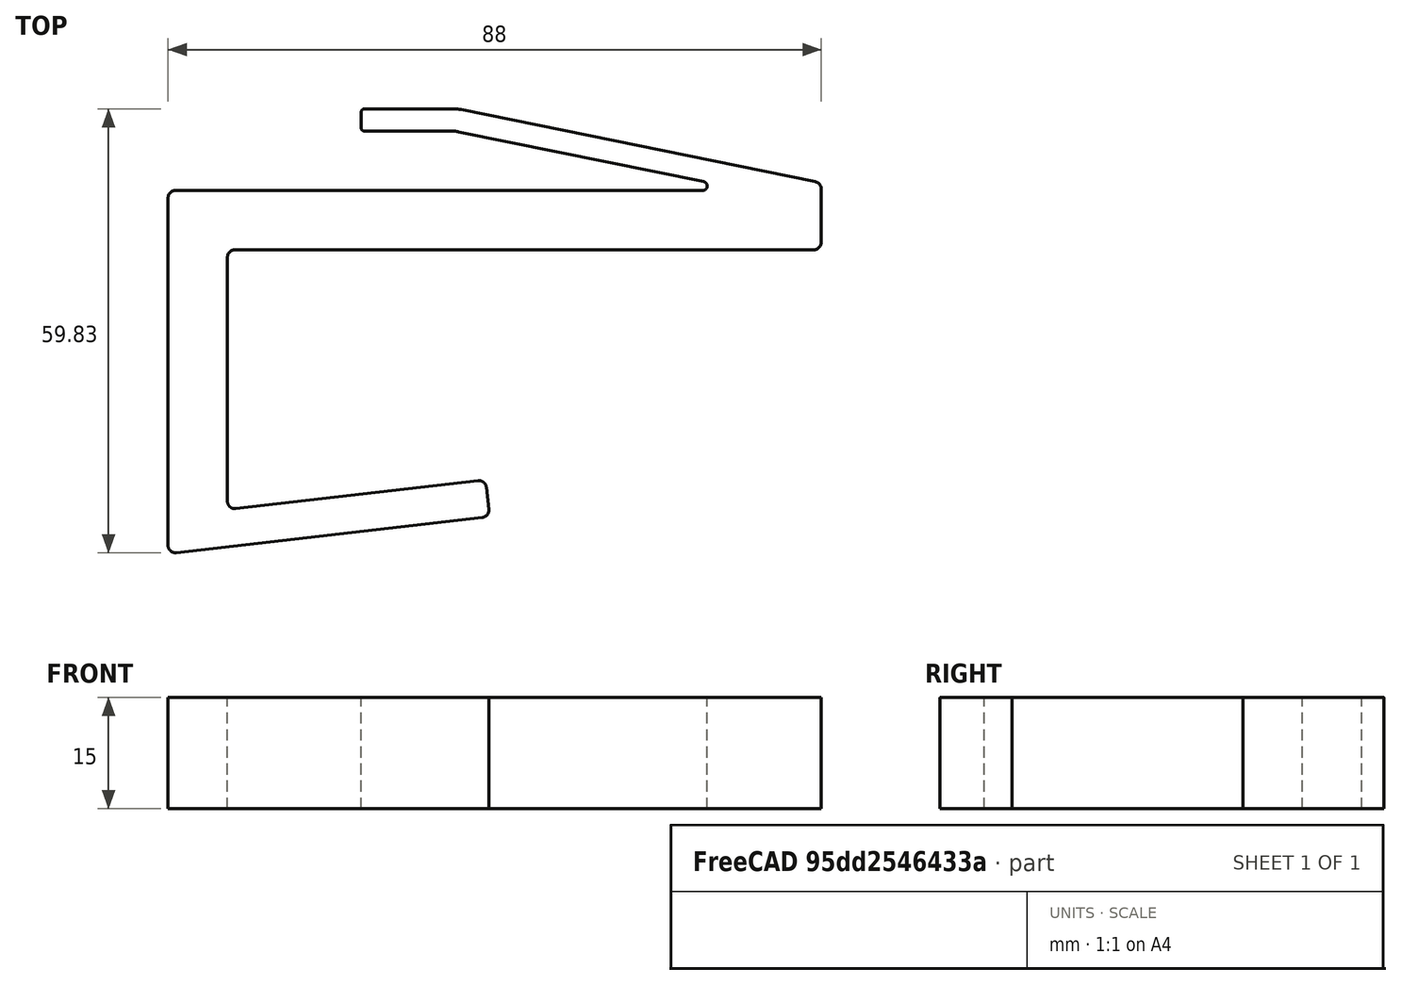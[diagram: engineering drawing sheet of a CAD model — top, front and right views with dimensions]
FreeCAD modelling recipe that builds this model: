
FCSTD DOCUMENT  (FreeCAD 0.16R)
Label: ClosetDoorLatch
License: All rights reserved
LicenseURL: http://en.wikipedia.org/wiki/All_rights_reserved
objects: PartDesign::Fillet×6, Sketcher::SketchObject×1, PartDesign::Pad×1, Mesh::Feature×1
note: 9 computed .brp shape members not serialized (recipe doc carries the construction recipe); baked Part::Feature solids carry a one-line shape summary decoded from their .brp

FEATURE [Sketcher::SketchObject] Sketch
  sketch-geometry (13):
    g0: LineSegment StartX=-8 StartY=8 StartZ=0 EndX=70 EndY=8 EndZ=0
    g1: LineSegment StartX=18 StartY=16 StartZ=0 EndX=18 EndY=19 EndZ=0
    g2: LineSegment StartX=18 StartY=19 StartZ=0 EndX=31 EndY=19 EndZ=0
    g3: LineSegment StartX=31 StartY=19 StartZ=0 EndX=80 EndY=9.02601 EndZ=0
    g4: LineSegment StartX=80 StartY=9.02601 StartZ=0 EndX=80 EndY=0 EndZ=0
    g5: LineSegment StartX=-8 StartY=-40.9533 StartZ=0 EndX=35.3421 EndY=-35.9672 EndZ=0
    g6: LineSegment StartX=35.3421 StartY=-35.9672 StartZ=0 EndX=34.7707 EndY=-31 EndZ=0
    g7: LineSegment StartX=34.7707 StartY=-31 StartZ=0 EndX=0 EndY=-35 EndZ=0
    g8: LineSegment StartX=0 StartY=-35 StartZ=0 EndX=0 EndY=0 EndZ=0
    g9: LineSegment StartX=0 StartY=0 StartZ=0 EndX=80 EndY=0 EndZ=0
    g10: LineSegment StartX=-8 StartY=8 StartZ=0 EndX=-8 EndY=-40.9533 EndZ=0
    g11: LineSegment StartX=18 StartY=16 StartZ=0 EndX=30.6978 EndY=16 EndZ=0
    g12: LineSegment StartX=30.6978 StartY=16 StartZ=0 EndX=70 EndY=8 EndZ=0
  constraints (39):
    c: PointOnObject(g4,g-1)
    c: Horizontal(g0)
    c: Coincident(g1,g2)
    c: Coincident(g2,g3)
    c: Distance(g1) = 3
    c: Vertical(g4)
    c: DistanceX(g4) = 80
    c: DistanceX(g1) = 18
    c: Vertical(g1)
    c: Distance(g2) = 13
    c: Coincident(g5,g6)
    c: Coincident(g6,g7)
    c: Coincident(g7,g8)
    c: Coincident(g8,g9)
    c: Coincident(g9,g4)
    c: Coincident(g10,g0)
    c: Coincident(g5,g10)
    c: Vertical(g10)
    c: Vertical(g8)
    c: Distance(g8,g10) = 8
    c: Distance(g8,g0) = 8
    c: PointOnObject(g8,g-1)
    c: Distance(g5,g7) = 5
    c: Distance(g6,g9) = 31
    c: Distance(g8) = 35
    c: Perpendicular(g6,g5)
    c: Distance(g7) = 35
    c: Coincident(g1,g11)
    c: Horizontal(g11)
    c: Coincident(g11,g12)
    c: Coincident(g12,g0)
    c: Distance(g1,g9) = 16
    c: Distance(g11,g2) = 3
    c: Parallel(g12,g3)
    c: Coincident(g4,g3)
    c: PointOnObject(g8,g-2)
    c: Distance(g0,g3) = 3
    c: Parallel(g5,g7)
    c: Distance(g0,g4) = 10
FEATURE [PartDesign::Pad] Pad
  Length = 15
  Length2 = 100
  Sketch = -> Sketch
  Type = 0
FEATURE [PartDesign::Fillet] Fillet
  Base = -> Pad [Edge2,Edge23,Edge20,Edge1,Edge32,Edge26,Edge29]
  Radius = 1
FEATURE [PartDesign::Fillet] Fillet001
  Base = -> Fillet [Edge45]
  Radius = 0.6
FEATURE [PartDesign::Fillet] Fillet002
  Base = -> Fillet001 [Edge33,Edge37]
  Radius = 0.5
FEATURE [PartDesign::Fillet] Fillet003
  Base = -> Fillet002 [Edge53]
  Radius = 1
FEATURE [PartDesign::Fillet] Fillet004
  Base = -> Fillet003 [Edge70]
  Radius = 5
FEATURE [PartDesign::Fillet] Fillet005
  Base = -> Fillet004 [Edge43]
  Radius = 5
FEATURE [Mesh::Feature] Mesh  label="Fillet005 (Meshed)"
